# Revit family: FP-Revit18-RDV3-488-L-DualFuelCooker-0-CA-US-90001812A (1)
name_source: partatom
category: Specialty Equipment
units: mm (PartAtom-declared; Revit-internal decimal feet)

## family parameters
Always vertical = Yes
Cut with Voids When Loaded = Yes
OmniClass Number = 23.40.40.14.17.17
OmniClass Title = Ranges
Part Type = Normal
Room Calculation Point = No
Round Connector Dimension = Use Diameter
Shared = No
Work Plane-Based = No

## types (2) — shared parameters
Cavity - Depth = 704 mm  [stored 2.30971 ft]
Cavity - Width = 1219 mm
Clearance - Overhead Combustible = 1372 mm  [stored 4.50131 ft]
Clearance - Overhead Non-Combustible = 762 mm  [stored 2.5 ft]
Clearance - Overhead Rangehood = 914 mm  [stored 2.99869 ft]
Clearance - Rear Combustible = 305 mm  [stored 1.00066 ft]
Clearance - Side Combustible = 305 mm  [stored 1.00066 ft]
Connector Note - Electrical = 120/208 V or 120/240 V, 60Hz, 50 amp fused electrical supply, 44 amp Max
Countertop Height (min 908mm - max 933mm) = 915 mm  [stored 3.00197 ft]
Description = Dual Fuel Range, 48", 8 Burners
Manufacturer = Fisher & Paykel Appliances
Material - Body = Fisher & Paykel - Stainless Steel
Material - Burner Pan = Fisher & Paykel - Black
Material - Burners & Trivets = Fisher & Paykel - Black, Matte
Material - Buttons and Dials = Fisher & Paykel - Aluminium, Dark
Material - Display Panel = Fisher & Paykel - Black
Material - Handle = Fisher & Paykel - Stainless Steel
Material - Trim = Fisher & Paykel - Aluminium
Product - Depth = 703 mm  [stored 2.30643 ft]
Product - Height = 915 mm  [stored 3.00197 ft]
Product - Width = 1216 mm  [stored 3.9895 ft]
URL = www.fisherpaykel.com
Visibility - Clearance Required = Yes
zero-valued in all types: Cavity - Height, Clearance - Rear Non-Combustible, Clearance - Side Non-Combustible, Default Elevation

## per-type parameters (varying)
| type | Connector Note - Gas |
| RDV3-488-N | NG 6" to 9" WC, with 1/2” NPT Minimum 5/8” dia. flex line |
| RDV3-488-L | LPG 11" to 14" WC, with 1/2” NPT Minimum 5/8” dia. flex line |

note: column(s) folded — value = type name in every type: Model

note: [stored X ft] marks values corroborated as IEEE doubles in the binary element streams (Revit-internal decimal feet)

## geometry (parser evidence)
native form markers: Sweep x17
no freeform markers — native parametric forms only
